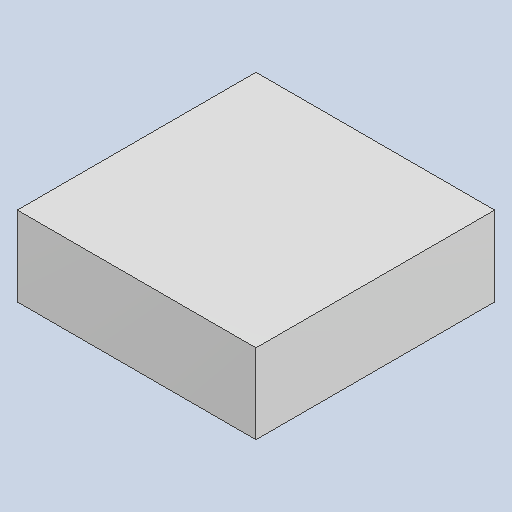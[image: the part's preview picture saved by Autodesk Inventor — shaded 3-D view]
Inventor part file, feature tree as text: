
AUTODESK INVENTOR PART (.ipt)
format: ipt  version: 2023.4 (Build 274418000, 418)  size: 79,872 bytes
history: native  units: mm
features: extrude x1
ambient origin geometry x8: Origin, YZ Plane, XZ Plane, XY Plane, X Axis, Y Axis, Z Axis, Center Point
bodies: Solid1 (feature_tree)
feature tree (1):
  extrude  "Extruded_22"  [1 undecoded]
note: 1 required parameter value undecoded (feature->parameter linkage not recoverable at this tier; creation-order binding heuristic only, values carry confidence <= 0.55)
